# Revit family: for update_72650SGP_new
name_source: partatom
category: Plumbing Fixtures
revit_build: Autodesk Revit 2018 (Build: 20170223_1515(x64)
units: mm (PartAtom-declared; Revit-internal decimal feet)

## family parameters
Always vertical = No
Cut with Voids When Loaded = No
OmniClass Number = 23.45.55.17
OmniClass Title = Mixing Faucets
Part Type = Normal
Room Calculation Point = No
Round Connector Dimension = Use Diameter
Shared = No
Work Plane-Based = Yes

## types (2) — shared parameters
Always visible = Yes
BIMobject category = Taps & Mixers
Cold Water Inlet = 13 mm
Cold Water Inlet Description = Cold Water Inlet 12.7mm
Default Elevation = 1219.2 mm  [stored 4 ft]
Description = Rebris E Single lever shower mixer for exposed installation 2 ticks
Design country = Germany
EAN code = 4059625401804
Edition number = 1
GTIN code = https://4059625401804
Hot Water Inlet = 13 mm
Hot Water Inlet Description = Hot Water Inlet 12.7mm
IFC Classification = Valve
Manufacturer = Hansgrohe
Manufacturer country = Germany
Manufacturer name = hansgrohe
Model = 72650SGP
OmniClass Code = 23-31 11 00
OmniClass Description = Faucets
Product Guid = 2a0161a9-4e90-4311-b8a4-2bc8d8d00571
Product SKU = 72650SGP
Product data url = https://bimobject.com
Product family = Rebris E
Product group = Shower mixers
Product name = 72650SGP Rebris E Single lever shower mixer for exposed installation 2 ticks
QR code = https://bimobject.com
UNSPSC Code = 301815
URL = https://www.hansgrohe.com
Weight Net (Kg) = 1.6

## per-type parameters (varying)
| type | Material 1 |
| 679 Matte Black | Hansgrohe - Metal - 679 Matte Black |
| 009 Chrome | Hansgrohe - Metal - 009 Chrome |

note: [stored X ft] marks values corroborated as IEEE doubles in the binary element streams (Revit-internal decimal feet)

## geometry (parser evidence)
native form markers: Sweep x2
no freeform markers — native parametric forms only
